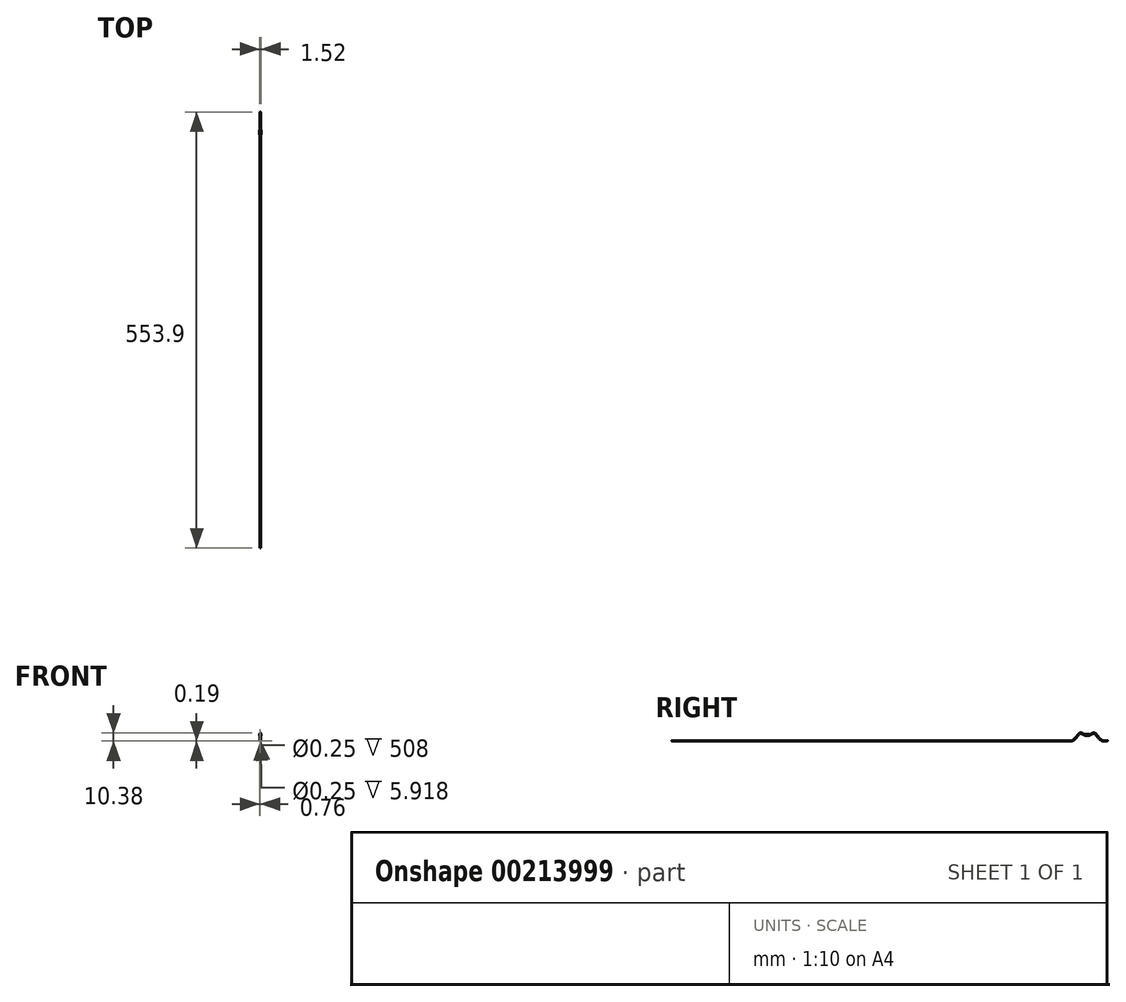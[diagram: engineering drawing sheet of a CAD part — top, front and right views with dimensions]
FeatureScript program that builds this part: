
annotation { "Feature Type Name" : "Feature", "Feature Type Description" : "" }
export const myFeature = defineFeature(function(context is Context, id is Id, definition is map)
    precondition{}
    {
        {
            var Q0;
            Q0=qCreatedBy(makeId("Right.planeOp"),FACE);
            var sketch = newSketch(context, id + "F0", { "sketchPlane" : qUnion([Q0])});
            skLineSegment(sketch, "E0", {"start": v(0, 0) * mm, "end": v(-5.92, 0) * mm});
            skFitSpline(sketch, "E1", {"points": [v(-5.92, 0) * mm, v(-11.66, 4.3) * mm, v(-15.89, 9.43) * mm, v(-19.56, 9.58) * mm, v(-22.86, 7.63) * mm], "startDerivative": vector(-13.48, 0) * mm, "endDerivative": vector(-16.63, 0) * mm});
            skLineSegment(sketch, "E2", {"start": v(-22.86, 7.63) * mm, "end": v(-28.96, 7.63) * mm});
            skLineSegment(sketch, "E3", {"start": v(-25.9, 37.72) * mm, "end": v(-25.9, -23.67) * mm, "construction": true});
            skPoint(sketch, "E4", {"position": v(-25.9, 7.63) * mm});
            skFitSpline(sketch, "E5.MirrorCS", {"points": [v(-45.9, 0) * mm, v(-40.16, 4.3) * mm, v(-35.93, 9.43) * mm, v(-32.26, 9.58) * mm, v(-28.96, 7.63) * mm], "startDerivative": vector(13.48, 0) * mm, "endDerivative": vector(16.63, 0) * mm});
            skLineSegment(sketch, "E6", {"start": v(-45.9, 0) * mm, "end": v(-553.9, 0) * mm});
            skLineSegment(sketch, "E7", {"start": v(-69.5, 10) * mm, "end": v(10.73, 10) * mm, "construction": true});
            skSolve(sketch);
        }
        {
            var Q0;
            Q0=qCreatedBy(makeId("Front.planeOp"),FACE);
            var sketch = newSketch(context, id + "F1", { "sketchPlane" : qUnion([Q0])});
            skCircle(sketch, "E8", {"center": v(0, -0.2) * mm, "radius": 0.2 * mm});
            skCircle(sketch, "E9", {"center": v(0, -0.2) * mm, "radius": 0.13 * mm});
            skSolve(sketch);
        }
        {
            var Q0;
            Q0=qSketchRegion(id+"F1",true);
            var Q1;
            Q1=qConstructionFilter(qBodyType(qCreatedBy(id+"F0",EDGE),BodyType.WIRE),ConstructionObject.NO);
            sweep(context, id + "F2", {"profiles" : qUnion([Q0]), "path" : qUnion([Q1])});
        }
        {
            var Q0;
            Q0=qCreatedBy(makeId("Front.planeOp"),FACE);
            cPlane(context, id + "F3", {"entities" : qUnion([Q0]), "cplaneType" : CPlaneType.OFFSET, "offset" : 22.86 * mm, "width" : 152.4 * mm, "height" : 152.4 * mm});
        }
        {
            var Q0;
            Q0=qCreatedBy(id+"F3.planeOp",FACE);
            var sketch = newSketch(context, id + "F4", { "sketchPlane" : qUnion([Q0])});
            skCircle(sketch, "E10.0", {"center": v(0, 7.44) * mm, "radius": 0.2 * mm, "construction": true});
            skCircle(sketch, "E11", {"center": v(0, 7.44) * mm, "radius": 0.76 * mm});
            skSolve(sketch);
        }
        {
            var Q0;
            Q0=qSketchRegion(id+"F4",true);
            extrude(context, id + "F5", {"entities" : qUnion([Q0]), "operationType" : NewBodyOperationType.ADD, "depth" : 6.1 * mm});
        }
    });
